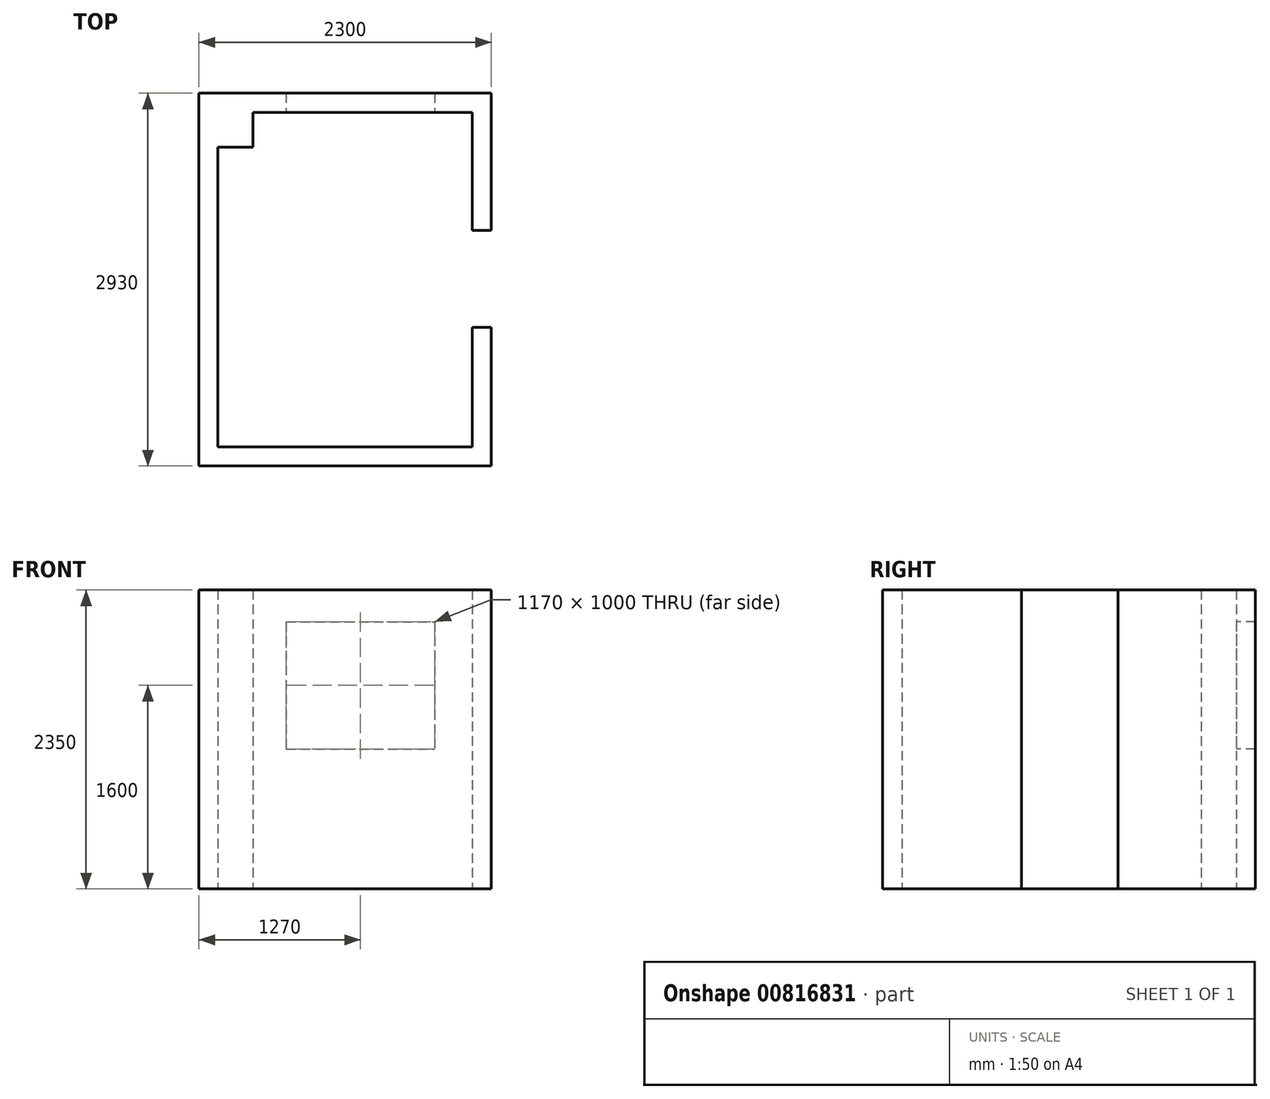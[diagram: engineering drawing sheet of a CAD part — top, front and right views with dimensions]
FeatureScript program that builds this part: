
annotation { "Feature Type Name" : "Feature", "Feature Type Description" : "" }
export const myFeature = defineFeature(function(context is Context, id is Id, definition is map)
    precondition{}
    {
        {
            var Q0;
            Q0=qCreatedBy(makeId("Top.planeOp"),FACE);
            var sketch = newSketch(context, id + "F0", { "sketchPlane" : qUnion([Q0])});
            skLineSegment(sketch, "E0", {"start": v(0, 0) * mm, "end": v(0, 940) * mm});
            skLineSegment(sketch, "E1", {"start": v(0, 940) * mm, "end": v(150, 940) * mm});
            skLineSegment(sketch, "E2", {"start": v(150, 940) * mm, "end": v(150, -150) * mm});
            skLineSegment(sketch, "E3", {"start": v(150, -150) * mm, "end": v(-2150, -150) * mm});
            skLineSegment(sketch, "E4", {"start": v(-2150, -150) * mm, "end": v(-2150, 2780) * mm});
            skLineSegment(sketch, "E5", {"start": v(-2150, 2780) * mm, "end": v(150, 2780) * mm});
            skLineSegment(sketch, "E6", {"start": v(150, 2780) * mm, "end": v(150, 1700) * mm});
            skLineSegment(sketch, "E7", {"start": v(150, 1700) * mm, "end": v(0, 1700) * mm});
            skLineSegment(sketch, "E8", {"start": v(0, 1700) * mm, "end": v(0, 2630) * mm});
            skLineSegment(sketch, "E9", {"start": v(0, 2630) * mm, "end": v(-1725, 2630) * mm});
            skLineSegment(sketch, "E10", {"start": v(-1725, 2630) * mm, "end": v(-1725, 2355) * mm});
            skLineSegment(sketch, "E11", {"start": v(-1725, 2355) * mm, "end": v(-2000, 2355) * mm});
            skLineSegment(sketch, "E12", {"start": v(-2000, 2355) * mm, "end": v(-2000, 0) * mm});
            skLineSegment(sketch, "E13", {"start": v(-2000, 0) * mm, "end": v(0, 0) * mm});
            skSolve(sketch);
        }
        {
            var Q0;
            Q0=makeQuery(id+"F0.imprint","IMPRINT",FACE,{"disambiguationData":[TD([[makeQuery(id+"F0.imprint","IMPRINT",EDGE,{"derivedFrom":sQuery(id+"F0.wireOp",EDGE,"E0")}),-1.0]])]});
            extrude(context, id + "F1", {"entities" : qUnion([Q0]), "depth" : 2350 * mm, "offsetDistance" : 25 * mm});
        }
        {
            var Q0;
            Q0=makeQuery(id+"F1.opExtrude","SWEPT_FACE",FACE,{"disambiguationData":[OSD([sQuery(id+"F0.wireOp",EDGE,"E9")])]});
            var sketch = newSketch(context, id + "F2", { "sketchPlane" : qUnion([Q0])});
            skLineSegment(sketch, "E14.bottom", {"start": v(-1465, 2100) * mm, "end": v(-295, 2100) * mm});
            skLineSegment(sketch, "E14.top", {"start": v(-1465, 1100) * mm, "end": v(-295, 1100) * mm});
            skLineSegment(sketch, "E14.left", {"start": v(-1465, 2100) * mm, "end": v(-1465, 1100) * mm});
            skLineSegment(sketch, "E14.right", {"start": v(-295, 2100) * mm, "end": v(-295, 1100) * mm});
            skSolve(sketch);
        }
        {
            var Q0;
            Q0 = qSketchRegion(id + "F2", true);
            extrude(context, id + "F3", {"entities" : qUnion([Q0]), "operationType" : NewBodyOperationType.REMOVE, "endBound" : BoundingType.UP_TO_NEXT, "oppositeDirection" : true, "depth" : 25 * mm, "offsetDistance" : 25 * mm});
        }
    });
